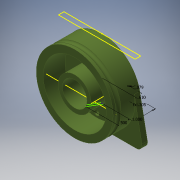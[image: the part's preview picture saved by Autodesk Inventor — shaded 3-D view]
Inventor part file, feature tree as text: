
AUTODESK INVENTOR PART (.ipt)
format: ipt  version: 2018 (Build 220112000, 112)  size: 359,936 bytes
history: native  units: in
note: dims shown in document units (in); Inventor stores cm internally (conversion verified against a paired STEP export)
features: sketch x17, extrude x13, reference x6, other x3, projected_geometry x2, revolve x1, mirror x1, fillet x1
ambient origin geometry x8: Origin, YZ Plane, XZ Plane, XY Plane, X Axis, Y Axis, Z Axis, Center Point
bodies: Solid1 (feature_tree)
feature tree (44):
  extrude  "Extrusion1"  Depth=3.5in
  extrude  "Extrusion2"  Depth=1.75in
  extrude  "Extrusion3"  Depth=0.25in TaperAngle=0.0deg
  extrude  "Extrusion4"  Depth=1.0in TaperAngle=0.0deg
  extrude  "Extrusion7"  Depth=1.5in TaperAngle=0.0deg
  revolve  "Revolution1"  [1 undecoded]
  sketch  "Sketch11"  dims[d26=1.0in d27=0.0in d28=0.1275in]
  sketch  "Sketch12"  dims[d31=0.75in d33=90.0deg]
  extrude  "Extrusion11"  Depth=0.1275in
  extrude  "Extrusion12"  TaperAngle=90.0deg  [1 undecoded]
  sketch  "Sketch15"  dims[d53=0.2953in d54=0.1181in]
  mirror  "Mirror2"
  extrude  "Extrusion14"  Depth=1.0in
  extrude  "Extrusion15"  Depth=3.5in
  extrude  "Extrusion16"  Depth=0.2953in
  extrude  "Extrusion17"  Depth=0.2953in
  extrude  "Extrusion18"  TaperAngle=15.0deg  [1 undecoded]
  extrude  "Extrusion19"  Depth=1.0in
  fillet  "Fillet1"  Radius=1.0in
  sketch  "Sketch1"  dims[d0=3.5in d1=3.5in]
  sketch  "Sketch2"  dims[d2=3.5in d3=1.75in]
  sketch  "Sketch3"  dims[d4=1.75in d5=0.25in d6=0.0in]
  sketch  "Sketch4"  dims[d8=0.0625in d9=1.0in d10=0.0in]
  sketch  "Sketch7"  dims[d11=1.125in d12=1.5in d13=0.0in]
  projected_geometry  "Projected Loop1"
  sketch  "Sketch8"  dims[d14=1.5in d15=1.0in d16=0.0in]
  projected_geometry  "Projected Loop4"
  sketch  "Sketch13"  dims[d43=1.0in d44=0.5in]
  sketch  "Sketch14"  dims[d45=0.0675in d46=3.5in]
  sketch  "Sketch16"  dims[d55=0.1181in d56=0.2953in]
  sketch  "Sketch17"  dims[d57=14.1732in d59=360.0deg d61=15.0deg]
  sketch  "Sketch18"  dims[d62=0.5256in d63=0.0in d64=0.2135in d69=1.0in d70=0.0in]
  reference  "Reference3"
  reference  "Reference4"
  sketch  "Sketch19"  dims[d71=1.25in]
  reference  "Reference5"
  reference  "Reference6"
  reference  "Reference7"
  reference  "Reference8"
  sketch  "Sketch20"  dims[d72=1.25in]
  sketch  "Sketch21"  dims[d73=1.25in d74=1.25in d75=2.375in d76=1.0in d77=0.3051in d78=0.6102in d79=0.0791in d82=2.875in d83=0.4685in d84=1.125in d85=1.0in d86=0.0in d87=0.05in d88=1.0in d89=0.0in d90=1.0in d91=0.0in d92=0.02in d93=0.1693in d94=0.0in d95=0.1181in d98=15.0deg d99=0.2953in d100=0.1181in d101=0.375in d102=0.375in d103=0.1693in d104=0.0in d105=0.1693in d106=0.0in d107=0.25in]
  parser-record x1  (decoder bookkeeping rows leaked as tree rows — omitted from the tree; the rows remain in map.json)
  other  "Assembly1.iam"
  other  "microServo-sg90:1"
note: 3 required parameter values undecoded (feature->parameter linkage not recoverable at this tier; creation-order binding heuristic only, values carry confidence <= 0.55)
note: 1 file-system path scrubbed to <path> (originals preserved in map.json)